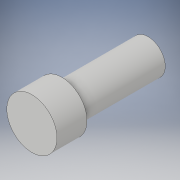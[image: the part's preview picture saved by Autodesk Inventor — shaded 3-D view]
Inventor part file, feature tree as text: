
AUTODESK INVENTOR PART (.ipt)
format: ipt  version: 2019 (Build 230136000, 136)  size: 100,352 bytes
history: native  units: in
note: dims shown in document units (in); Inventor stores cm internally (conversion verified against a paired STEP export)
features: extrude x2, sketch x2
ambient origin geometry x8: Origin, YZ Plane, XZ Plane, XY Plane, X Axis, Y Axis, Z Axis, Center Point
bodies: Solid1 (feature_tree)
feature tree (4):
  extrude  "Extrusion1"  Depth=0.385in TaperAngle=0.0deg
  extrude  "Extrusion2"  Depth=0.134in TaperAngle=0.0deg
  sketch  "Sketch1"  dims[d0=0.153in d1=0.385in d2=0.0in]
  sketch  "Sketch2"  dims[d3=0.224in d4=0.134in d5=0.0in]
